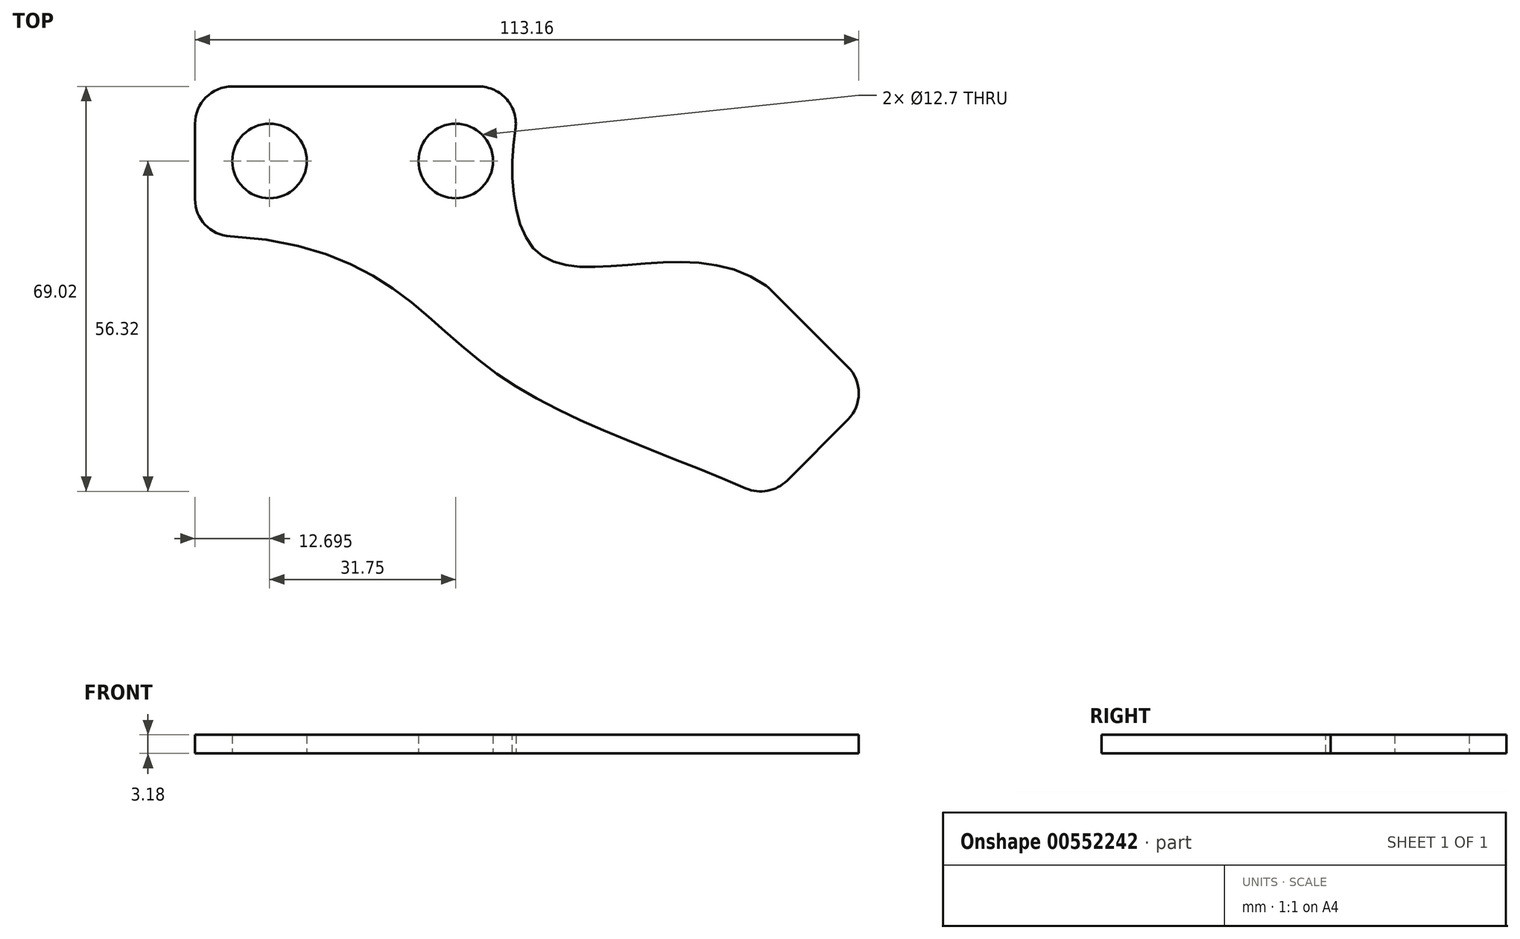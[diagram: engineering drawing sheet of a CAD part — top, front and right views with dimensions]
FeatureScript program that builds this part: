
annotation { "Feature Type Name" : "Feature", "Feature Type Description" : "" }
export const myFeature = defineFeature(function(context is Context, id is Id, definition is map)
    precondition{}
    {
        {
            var Q0;
            Q0=qCreatedBy(makeId("Top.planeOp"),FACE);
            var sketch = newSketch(context, id + "F0", { "sketchPlane" : qUnion([Q0])});
            skPoint(sketch, "E0.middle", {"position": v(0, 0) * mm});
            skLineSegment(sketch, "E1", {"start": v(47.35, -21.95) * mm, "end": v(60.5, -35.1) * mm});
            skLineSegment(sketch, "E2", {"start": v(60.5, -44.09) * mm, "end": v(50.13, -54.46) * mm});
            skLineSegment(sketch, "E3", {"start": v(-50.8, -6.5) * mm, "end": v(-50.8, 0) * mm});
            skCircle(sketch, "E4", {"center": v(-38.1, 0) * mm, "radius": 6.35 * mm});
            skCircle(sketch, "E5", {"center": v(-6.34, 0) * mm, "radius": 6.35 * mm});
            skFitSpline(sketch, "E6", {"points": [v(6.36, 12.7) * mm, v(7.6, -15.58) * mm, v(47.04, -21.64) * mm], "startDerivative": vector(-22.52, -28.96) * mm, "endDerivative": vector(69.84, -54.01) * mm});
            skLineSegment(sketch, "E7", {"start": v(-44.44, 12.7) * mm, "end": v(-2.44, 12.7) * mm});
            skFitSpline(sketch, "E8", {"points": [v(-50.8, -12.7) * mm, v(0, -35.81) * mm, v(47.04, -57.56) * mm], "startDerivative": vector(181.2, 1.66) * mm, "endDerivative": vector(94.9, -44.05) * mm});
            skArc(sketch, "E9.filletArc", {"start": v(3.82, 5.3) * mm, "mid": v(2.4, 10.45) * mm, "end": v(-2.44, 12.7) * mm});
            skArc(sketch, "E10.filletArc", {"start": v(-44.44, 12.7) * mm, "mid": v(-48.93, 10.84) * mm, "end": v(-50.8, 6.35) * mm});
            skArc(sketch, "E11.filletArc", {"start": v(-50.8, -6.5) * mm, "mid": v(-49.06, -10.86) * mm, "end": v(-44.8, -12.84) * mm});
            skArc(sketch, "E12.filletArc", {"start": v(43.11, -55.8) * mm, "mid": v(46.83, -56.21) * mm, "end": v(50.13, -54.46) * mm});
            skArc(sketch, "E13.filletArc", {"start": v(60.5, -44.09) * mm, "mid": v(62.37, -39.6) * mm, "end": v(60.5, -35.1) * mm});
            skArc(sketch, "E14.filletArc", {"start": v(47.35, -21.95) * mm, "mid": v(46.99, -21.62) * mm, "end": v(46.6, -21.3) * mm});
            skLineSegment(sketch, "E15", {"start": v(-50.8, 0) * mm, "end": v(-50.8, 6.35) * mm});
            skSolve(sketch);
        }
        {
            var Q0;
            Q0=makeQuery(id+"F0.imprint","IMPRINT",FACE,{"disambiguationData":[TD([[makeQuery(id+"F0.imprint","IMPRINT",EDGE,{"derivedFrom":sQuery(id+"F0.wireOp",EDGE,"E1")}),-1.0]])]});
            extrude(context, id + "F1", {"entities" : qUnion([Q0]), "depth" : 3.17 * mm, "offsetDistance" : 25.4 * mm});
        }
    });
